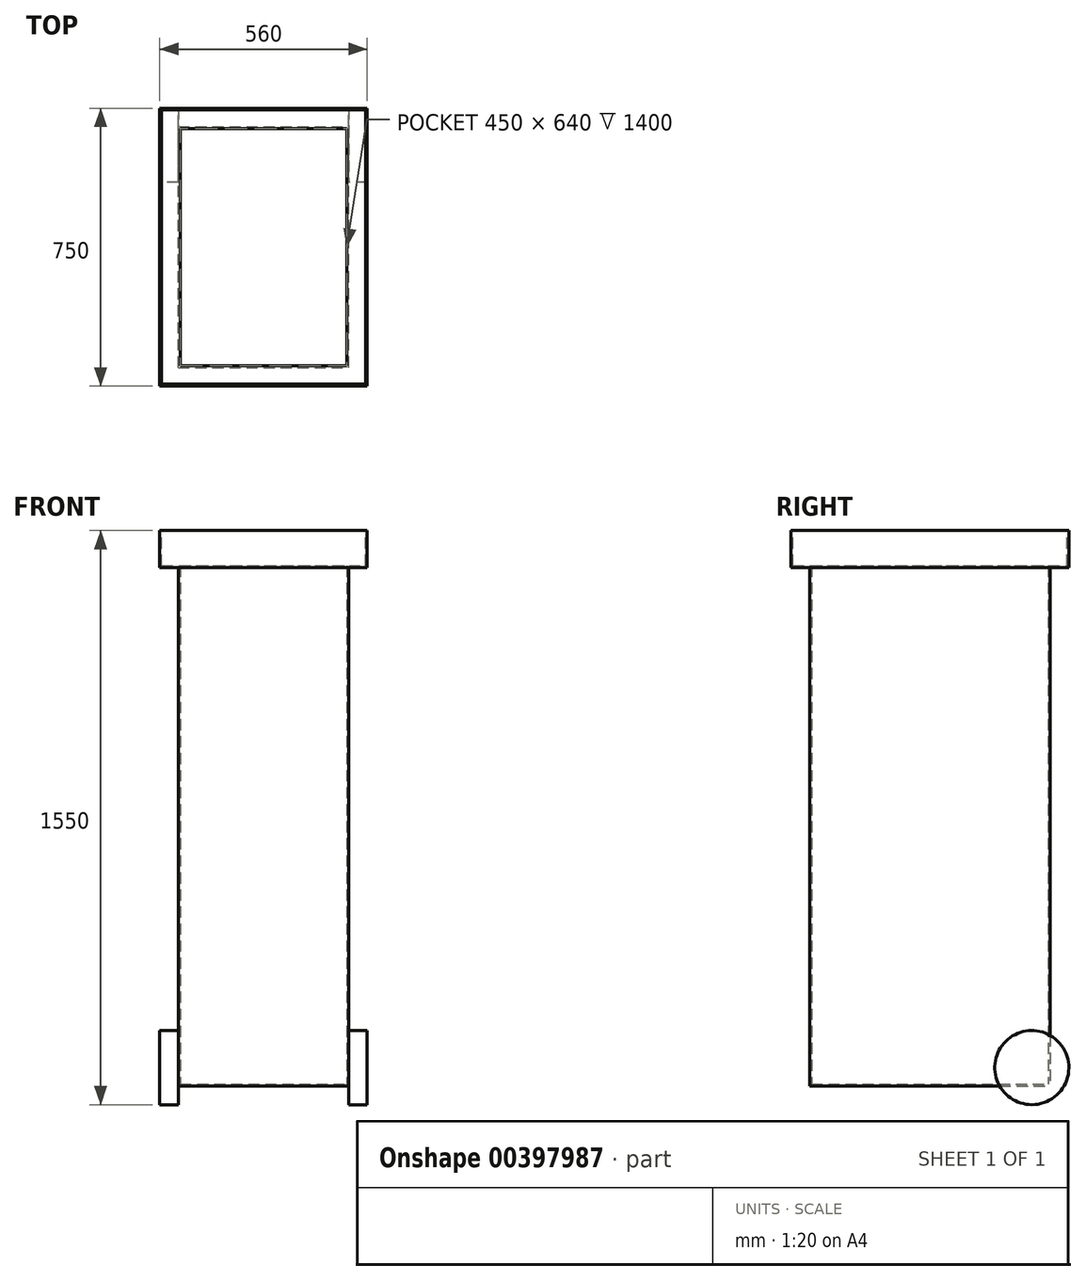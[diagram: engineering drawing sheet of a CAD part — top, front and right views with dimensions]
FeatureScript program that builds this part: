
annotation { "Feature Type Name" : "Feature", "Feature Type Description" : "" }
export const myFeature = defineFeature(function(context is Context, id is Id, definition is map)
    precondition{}
    {
        {
            var Q0;
            Q0=qCreatedBy(makeId("Top.planeOp"),FACE);
            cPlane(context, id + "F0", {"entities" : qUnion([Q0]), "cplaneType" : CPlaneType.OFFSET, "offset" : 50 * mm, "width" : 150 * mm, "height" : 150 * mm});
        }
        {
            var Q0;
            Q0=qCreatedBy(id+"F0.planeOp",FACE);
            var sketch = newSketch(context, id + "F1", { "sketchPlane" : qUnion([Q0])});
            skLineSegment(sketch, "E0.bottom", {"start": v(0, 0) * mm, "end": v(560, 0) * mm});
            skLineSegment(sketch, "E0.top", {"start": v(0, 750) * mm, "end": v(560, 750) * mm});
            skLineSegment(sketch, "E0.left", {"start": v(0, 0) * mm, "end": v(0, 750) * mm});
            skLineSegment(sketch, "E0.right", {"start": v(560, 0) * mm, "end": v(560, 750) * mm});
            skLineSegment(sketch, "E1.0", {"start": v(50, 50) * mm, "end": v(510, 50) * mm});
            skLineSegment(sketch, "E1.1", {"start": v(50, 50) * mm, "end": v(50, 700) * mm});
            skLineSegment(sketch, "E1.2", {"start": v(50, 700) * mm, "end": v(510, 700) * mm});
            skLineSegment(sketch, "E1.3", {"start": v(510, 50) * mm, "end": v(510, 700) * mm});
            skSolve(sketch);
        }
        {
            var Q0;
            Q0=makeQuery(id+"F1.imprint","IMPRINT",FACE,{"disambiguationData":[TD([[makeQuery(id+"F1.imprint","IMPRINT",EDGE,{"derivedFrom":sQuery(id+"F1.wireOp",EDGE,"E1.0")}),1.0]])]});
            extrude(context, id + "F2", {"entities" : qUnion([Q0]), "depth" : 1500 * mm});
        }
        {
            var Q0;
            Q0=makeQuery(id+"F2.opExtrude","CAP_FACE",FACE,{"disambiguationData":[OSD([sQuery(id+"F1.wireOp",EDGE,"E1.0"),sQuery(id+"F1.wireOp",EDGE,"E1.1"),sQuery(id+"F1.wireOp",EDGE,"E1.2"),sQuery(id+"F1.wireOp",EDGE,"E1.3")])],"isStart":false});
            var sketch = newSketch(context, id + "F3", { "sketchPlane" : qUnion([Q0])});
            skLineSegment(sketch, "E2.0", {"start": v(0, 0) * mm, "end": v(560, 0) * mm});
            skLineSegment(sketch, "E3.0", {"start": v(560, 0) * mm, "end": v(560, 750) * mm});
            skLineSegment(sketch, "E4.0", {"start": v(0, 750) * mm, "end": v(560, 750) * mm});
            skLineSegment(sketch, "E5.0", {"start": v(0, 0) * mm, "end": v(0, 750) * mm});
            skSolve(sketch);
        }
        {
            var Q0;
            Q0=makeQuery(id+"F3.imprint","IMPRINT",FACE,{"disambiguationData":[TD([[makeQuery(id+"F3.imprint","IMPRINT",EDGE,{"derivedFrom":sQuery(id+"F3.wireOp",EDGE,"E2.0")}),1.0]])]});
            extrude(context, id + "F4", {"entities" : qUnion([Q0]), "operationType" : NewBodyOperationType.ADD, "oppositeDirection" : true, "depth" : 100 * mm});
        }
        {
            var Q0;
            {var subQ0=sQuery(id+"F1.wireOp",EDGE,"E1.3");var subQ1=sQuery(id+"F1.wireOp",EDGE,"E1.2");var subQ2=sQuery(id+"F1.wireOp",EDGE,"E1.1");var subQ3=sQuery(id+"F1.wireOp",EDGE,"E1.0");Q0=makeQuery(id+"F4.boolean.opBoolean","MERGE",FACE,{"derivedFrom":[makeQuery(id+"F2.opExtrude","CAP_FACE",FACE,{"disambiguationData":[OSD([subQ3,subQ2,subQ1,subQ0])],"isStart":false}),makeQuery(id+"F4.opExtrude","CAP_FACE",FACE,{"disambiguationData":[OSD([subQ3,subQ2,subQ1,subQ0,sQuery(id+"F3.wireOp",EDGE,"E2.0"),sQuery(id+"F3.wireOp",EDGE,"E3.0"),sQuery(id+"F3.wireOp",EDGE,"E4.0"),sQuery(id+"F3.wireOp",EDGE,"E5.0")])],"isStart":true})]});}
            shell(context, id + "F5", {"entities" : qUnion([Q0]), "thickness" : 5 * mm});
        }
        {
            var Q0;
            Q0=qCreatedBy(makeId("Right.planeOp"),FACE);
            var sketch = newSketch(context, id + "F6", { "sketchPlane" : qUnion([Q0])});
            skCircle(sketch, "E6", {"center": v(650, 100) * mm, "radius": 100 * mm});
            skSolve(sketch);
        }
        {
            var Q0;
            Q0=makeQuery(id+"F6.imprint","IMPRINT",FACE,{"disambiguationData":[TD([[makeQuery(id+"F6.imprint","IMPRINT",EDGE,{"derivedFrom":sQuery(id+"F6.wireOp",EDGE,"E6")}),1.0]])]});
            var Q1;
            Q1=makeQuery(id+"F2.opExtrude","SWEPT_FACE",FACE,{"disambiguationData":[OSD([sQuery(id+"F1.wireOp",EDGE,"E1.1")])]});
            extrude(context, id + "F7", {"entities" : qUnion([Q0]), "operationType" : NewBodyOperationType.ADD, "endBound" : BoundingType.UP_TO_SURFACE, "endBoundEntityFace" : qUnion([Q1]), "depth" : 25 * mm});
        }
        {
            var Q0;
            Q0=makeQuery(id+"F2.opExtrude","SWEPT_FACE",FACE,{"disambiguationData":[OSD([sQuery(id+"F1.wireOp",EDGE,"E1.3")])]});
            var sketch = newSketch(context, id + "F8", { "sketchPlane" : qUnion([Q0])});
            skCircle(sketch, "E7.0", {"center": v(650, 100) * mm, "radius": 100 * mm});
            skSolve(sketch);
        }
        {
            var Q0;
            {var subQ0=sQuery(id+"F8.wireOp",EDGE,"E7.0");var subQ1=sQuery(id+"F1.wireOp",EDGE,"E1.3");var subQ2=makeQuery(id+"F2.opExtrude","CAP_EDGE",EDGE,{"disambiguationData":[OSD([subQ1])],"isStart":true});var subQ3=makeQuery(id+"F8.imprint","INTERSECT",VERTEX,{"derivedFrom":[subQ2,subQ0]});Q0=makeQuery(id+"F8.imprint","IMPRINT",FACE,{"disambiguationData":[TD([[makeQuery(id+"F8.imprint","IMPRINT",EDGE,{"disambiguationData":[TD([[subQ3,-1.0]])],"derivedFrom":subQ0}),1.0]])]});}
            var Q1;
            {var subQ0=sQuery(id+"F8.wireOp",EDGE,"E7.0");var subQ1=sQuery(id+"F1.wireOp",EDGE,"E1.3");var subQ2=makeQuery(id+"F2.opExtrude","CAP_EDGE",EDGE,{"disambiguationData":[OSD([subQ1])],"isStart":true});var subQ3=makeQuery(id+"F8.imprint","INTERSECT",VERTEX,{"derivedFrom":[subQ2,subQ0]});Q1=makeQuery(id+"F8.imprint","IMPRINT",FACE,{"disambiguationData":[TD([[makeQuery(id+"F8.imprint","IMPRINT",EDGE,{"disambiguationData":[TD([[subQ3,1.0]])],"derivedFrom":subQ0}),1.0]])]});}
            var Q2;
            Q2=makeQuery(id+"F4.opExtrude","SWEPT_FACE",FACE,{"disambiguationData":[OSD([sQuery(id+"F3.wireOp",EDGE,"E3.0")])]});
            extrude(context, id + "F9", {"entities" : qUnion([Q0, Q1]), "operationType" : NewBodyOperationType.ADD, "endBound" : BoundingType.UP_TO_SURFACE, "endBoundEntityFace" : qUnion([Q2]), "depth" : 25 * mm});
        }
    });
